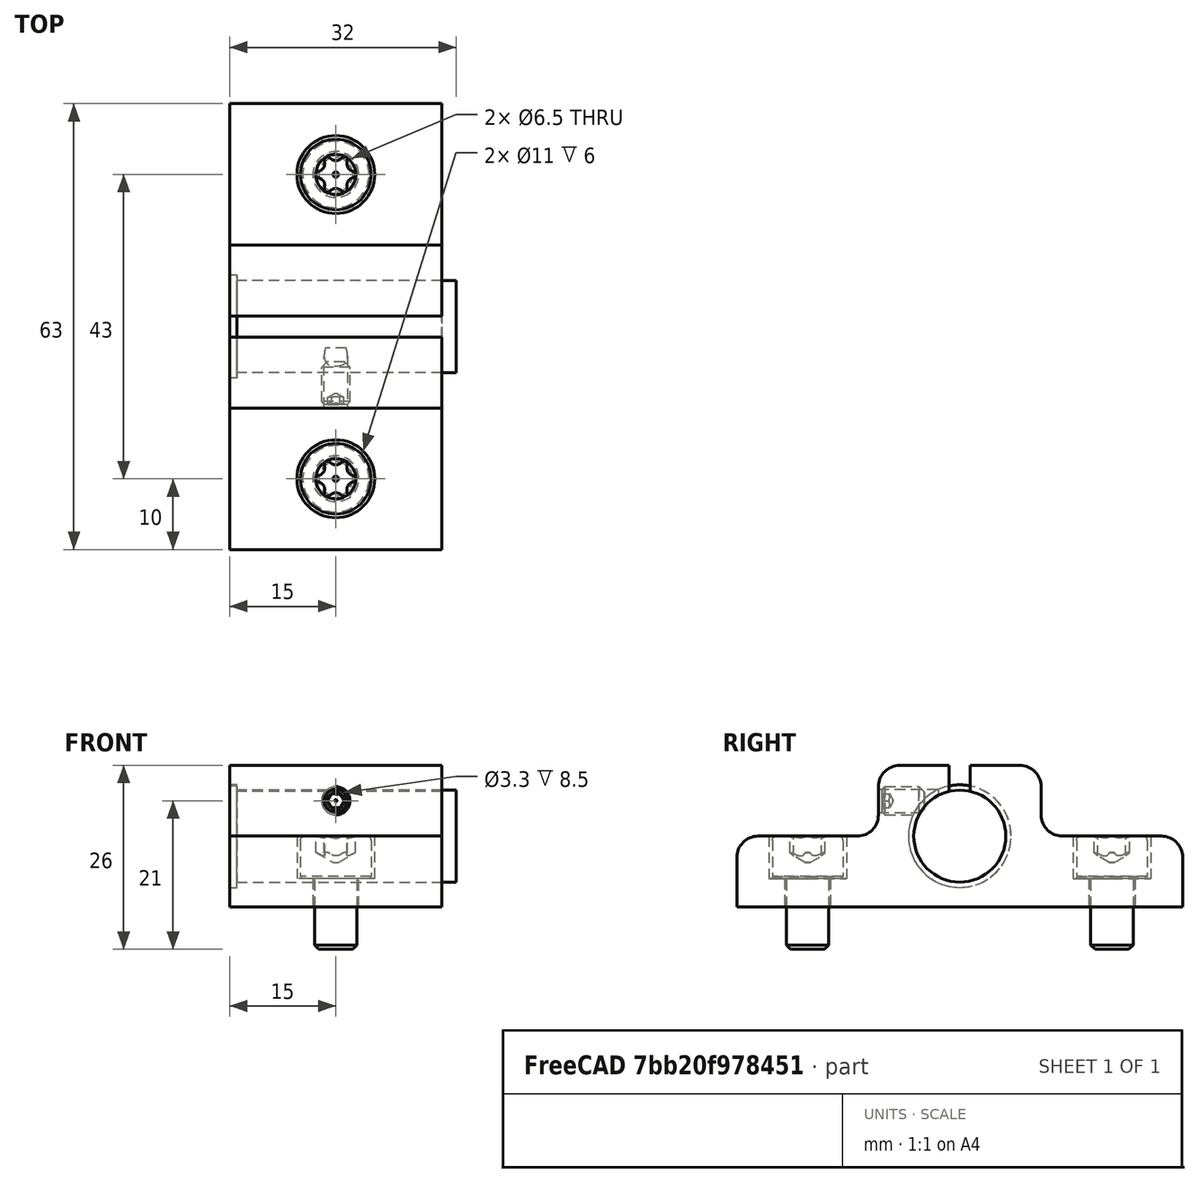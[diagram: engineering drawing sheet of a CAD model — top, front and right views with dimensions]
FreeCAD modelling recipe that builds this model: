
FCSTD DOCUMENT  (FreeCAD 0.22R0.21.2)
Label: LaserGridModuleMount
License: All rights reserved
LicenseURL: http://en.wikipedia.org/wiki/All_rights_reserved
objects: Part::Cylinder×9, Part::MultiFuse×6, Part::Cut×5, Part::Box×4, Part::FeaturePython×3, Part::Fillet×1, Part::Feature×1
note: 29 computed .brp shape members not serialized (recipe doc carries the construction recipe); baked Part::Feature solids carry a one-line shape summary decoded from their .brp

FEATURE [Part::Cylinder] Cylinder
  Angle = 360
  AttacherType = Attacher::AttachEngine3D
  FirstAngle = 0
  Height = 32
  Radius = 6.5
  SecondAngle = 0
FEATURE [Part::Cylinder] Cylinder001
  Angle = 360
  AttacherType = Attacher::AttachEngine3D
  FirstAngle = 0
  Height = 1
  Radius = 7.25
  SecondAngle = 0
FEATURE [Part::MultiFuse] Fusion  label="LaserModuleTemplate"
  Placement = pos=(-15,0,10) rot=(0,1,0;1.5708rad)
  Shapes = -> [Cylinder,Cylinder001]
FEATURE [Part::Box] Box  label="Cube"
  AttacherType = Attacher::AttachEngine3D
  Height = 20
  Length = 30
  Placement = pos=(-15,-31.5,0) rot=(0,0,1;0rad)
  Width = 63
FEATURE [Part::Cylinder] Cylinder002
  Angle = 360
  AttacherType = Attacher::AttachEngine3D
  FirstAngle = 0
  Height = 6
  Placement = pos=(0,0,4) rot=(0,0,1;0rad)
  Radius = 5.5
  SecondAngle = 0
FEATURE [Part::Cylinder] Cylinder003
  Angle = 360
  AttacherType = Attacher::AttachEngine3D
  FirstAngle = 0
  Height = 10
  Radius = 3.25
  SecondAngle = 0
FEATURE [Part::MultiFuse] Fusion001  label="ScrewThrough001"
  Placement = pos=(0,-21.5,0) rot=(0,0,1;0rad)
  Shapes = -> [Cylinder002,Cylinder003]
FEATURE [Part::Cylinder] Cylinder004
  Angle = 360
  AttacherType = Attacher::AttachEngine3D
  FirstAngle = 0
  Height = 6
  Placement = pos=(0,0,4) rot=(0,0,1;0rad)
  Radius = 5.5
  SecondAngle = 0
FEATURE [Part::Cylinder] Cylinder005
  Angle = 360
  AttacherType = Attacher::AttachEngine3D
  FirstAngle = 0
  Height = 10
  Radius = 3.25
  SecondAngle = 0
FEATURE [Part::MultiFuse] Fusion002  label="ScrewThrough002"
  Placement = pos=(0,21.5,0) rot=(0,0,1;0rad)
  Shapes = -> [Cylinder004,Cylinder005]
FEATURE [Part::Box] Box001  label="Cube001"
  AttacherType = Attacher::AttachEngine3D
  Height = 20
  Length = 30
  Placement = pos=(-15,11.5,10) rot=(0,0,1;0rad)
  Width = 20
FEATURE [Part::Box] Box002  label="Cube002"
  AttacherType = Attacher::AttachEngine3D
  Height = 20
  Length = 30
  Placement = pos=(-15,-31.5,10) rot=(0,0,1;0rad)
  Width = 20
FEATURE [Part::MultiFuse] Fusion003
  Shapes = -> [Box001,Box002]
FEATURE [Part::Cut] Cut
  Base = -> Box
  Tool = -> Fusion003
FEATURE [Part::MultiFuse] Fusion004
  Shapes = -> [Fusion002,Fusion001]
FEATURE [Part::Cut] Cut001
  Base = -> Cut
  Tool = -> Fusion004
FEATURE [Part::Box] Box003  label="Cube003"
  AttacherType = Attacher::AttachEngine3D
  Height = 15
  Length = 30
  Placement = pos=(-15,-1.5,15) rot=(0,0,1;0rad)
  Width = 3
FEATURE [Part::Cut] Cut002
  Base = -> Cut001
  Tool = -> Box003
FEATURE [Part::Cylinder] Cylinder006
  Angle = 360
  AttacherType = Attacher::AttachEngine3D
  FirstAngle = 0
  Height = 32
  Radius = 6.5
  SecondAngle = 0
FEATURE [Part::Cylinder] Cylinder007
  Angle = 360
  AttacherType = Attacher::AttachEngine3D
  FirstAngle = 0
  Height = 1
  Radius = 7.25
  SecondAngle = 0
FEATURE [Part::MultiFuse] Fusion005  label="LaserModuleTemplate001"
  Placement = pos=(-15,0,10) rot=(0,1,0;1.5708rad)
  Shapes = -> [Cylinder006,Cylinder007]
FEATURE [Part::Cut] Cut003  label="BlankNoRound"
  Base = -> Cut002
  Tool = -> Fusion005
FEATURE [Part::Fillet] Fillet
  Base = -> Cut003
  Edges = 6 edges r=3: [Edge15,Edge17,Edge21,Edge36,Edge39,Edge40]
FEATURE [Part::Cylinder] Cylinder008  label="M4WormScrew"
  Angle = 360
  AttacherType = Attacher::AttachEngine3D
  FirstAngle = 0
  Height = 10
  Placement = pos=(0,-3,15) rot=(1,0,0;1.5708rad)
  Radius = 1.65
  SecondAngle = 0
FEATURE [Part::Cut] Cut004
  Base = -> Fillet
  Tool = -> Cylinder008
FEATURE [Part::FeaturePython] Screw  label="M6x10-Screw"  # WARN: FeaturePython — macro-defined, semantics opaque (R4)
  Diameter = 6
  Invert = false
  LeftHanded = false
  Length = 0
  LengthCustom = 10
  MatchOuter = false
  Placement = pos=(0,-21.5,4) rot=(0,0,1;0rad)
  Thread = false
  Type = 52
FEATURE [Part::FeaturePython] Screw001  label="M6x10-Screw001"  # WARN: FeaturePython — macro-defined, semantics opaque (R4)
  Diameter = 6
  Invert = false
  LeftHanded = false
  Length = 0
  LengthCustom = 10
  MatchOuter = false
  Placement = pos=(0,21.5,4) rot=(0,0,1;0rad)
  Thread = false
  Type = 52
FEATURE [Part::FeaturePython] Screw002  label="M4x6-Screw"  # WARN: FeaturePython — macro-defined, semantics opaque (R4)
  Diameter = 7
  Invert = false
  LeftHanded = false
  Length = 2
  LengthCustom = 6
  MatchOuter = false
  Placement = pos=(0,-11,15) rot=(1,0,0;1.5708rad)
  Thread = false
  Type = 69
FEATURE [Part::Feature] Cut004_solid  label="LaserGridModuleMount_Solid"
  shape: bbox 30 x 63 x 20 mm, 32 faces (baked)
